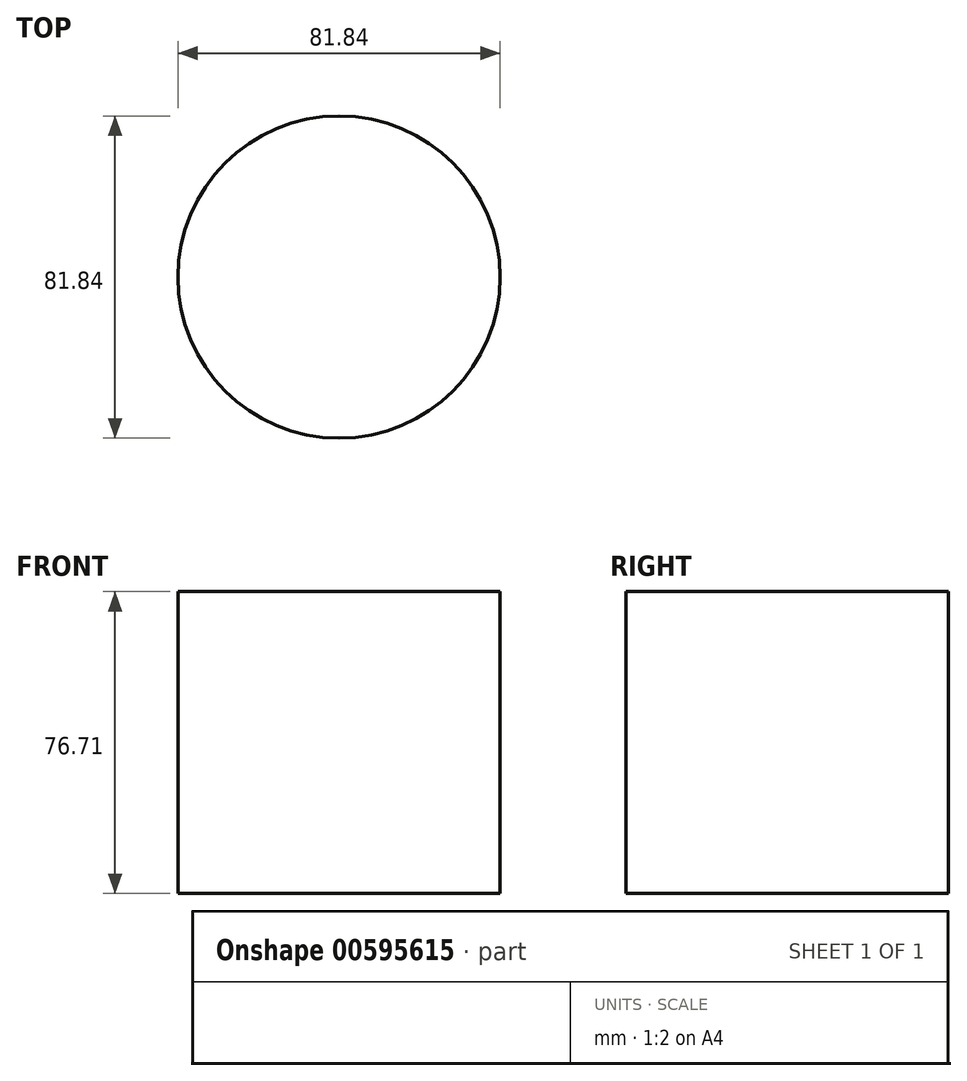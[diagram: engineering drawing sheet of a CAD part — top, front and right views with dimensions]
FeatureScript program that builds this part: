
annotation { "Feature Type Name" : "Feature", "Feature Type Description" : "" }
export const myFeature = defineFeature(function(context is Context, id is Id, definition is map)
    precondition{}
    {
        {
            var Q0;
            Q0=qCreatedBy(makeId("Top.planeOp"),FACE);
            var sketch = newSketch(context, id + "F0", { "sketchPlane" : qUnion([Q0])});
            skCircle(sketch, "E0", {"center": v(0, 0) * mm, "radius": 40.92 * mm});
            skSolve(sketch);
        }
        {
            var Q0;
            Q0=makeQuery(id+"F0.imprint","IMPRINT",FACE,{"disambiguationData":[TD([[makeQuery(id+"F0.imprint","IMPRINT",EDGE,{"derivedFrom":sQuery(id+"F0.wireOp",EDGE,"E0")}),1.0]])]});
            extrude(context, id + "F1", {"entities" : qUnion([Q0]), "depth" : 76.7 * mm, "offsetDistance" : 25.4 * mm});
        }
    });
